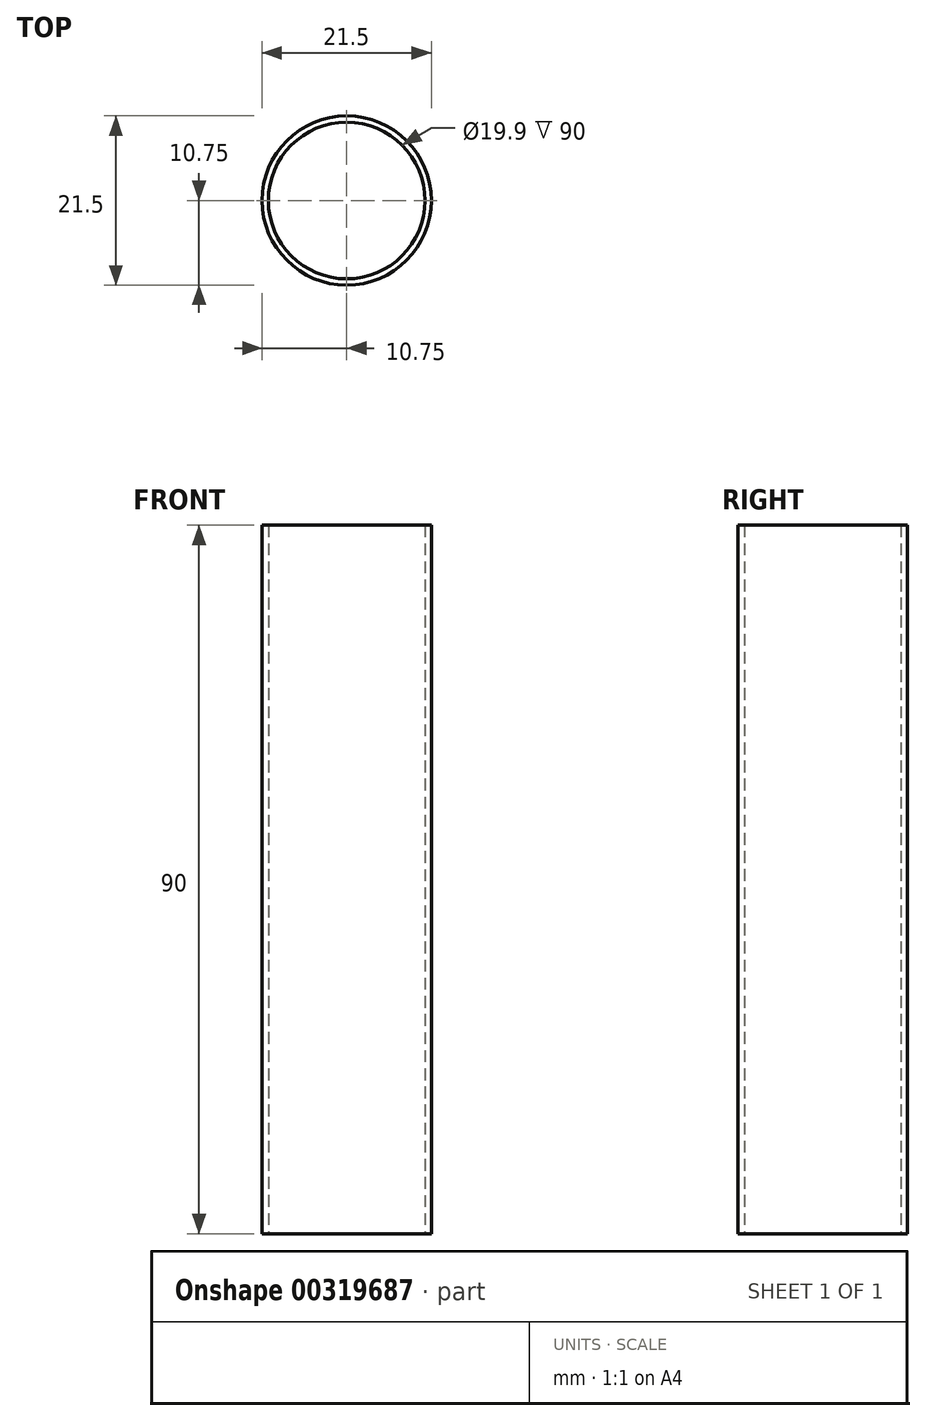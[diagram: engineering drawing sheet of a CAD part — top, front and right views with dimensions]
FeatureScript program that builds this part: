
annotation { "Feature Type Name" : "Feature", "Feature Type Description" : "" }
export const myFeature = defineFeature(function(context is Context, id is Id, definition is map)
    precondition{}
    {
        {
            var Q0;
            Q0=qCreatedBy(makeId("Top.planeOp"),FACE);
            var sketch = newSketch(context, id + "F0", { "sketchPlane" : qUnion([Q0])});
            skCircle(sketch, "E0", {"center": v(0, 0) * mm, "radius": 9.95 * mm});
            skCircle(sketch, "E1", {"center": v(0, 0) * mm, "radius": 10.75 * mm});
            skEllipse(sketch, "E2", {"center": v(0, 0) * mm, "majorRadius": 13 * mm, "minorRadius": 18.5 * mm, "majorAxis": v(-1, 0)});
            skCircle(sketch, "E3", {"center": v(7.75, 0) * mm, "radius": 2.5 * mm});
            skSolve(sketch);
        }
        {
            var Q0;
            Q0=makeQuery(id+"F0.imprint","IMPRINT",FACE,{"disambiguationData":[TD([[makeQuery(id+"F0.imprint","IMPRINT",EDGE,{"derivedFrom":sQuery(id+"F0.wireOp",EDGE,"E1")}),1.0]])]});
            var Q1;
            {var subQ0=sQuery(id+"F0.wireOp",EDGE,"E3");var subQ1=sQuery(id+"F0.wireOp",EDGE,"E0");var subQ2=makeQuery(id+"F0.imprint","INTERSECT",VERTEX,{"disambiguationData":[OD(0.0)],"derivedFrom":[subQ1,subQ0]});Q1=makeQuery(id+"F0.imprint","IMPRINT",FACE,{"disambiguationData":[TD([[makeQuery(id+"F0.imprint","IMPRINT",EDGE,{"disambiguationData":[TD([[subQ2,-1.0]])],"derivedFrom":subQ1}),-1.0]])]});}
            extrude(context, id + "F1", {"entities" : qUnion([Q0, Q1]), "depth" : 90 * mm});
        }
    });
